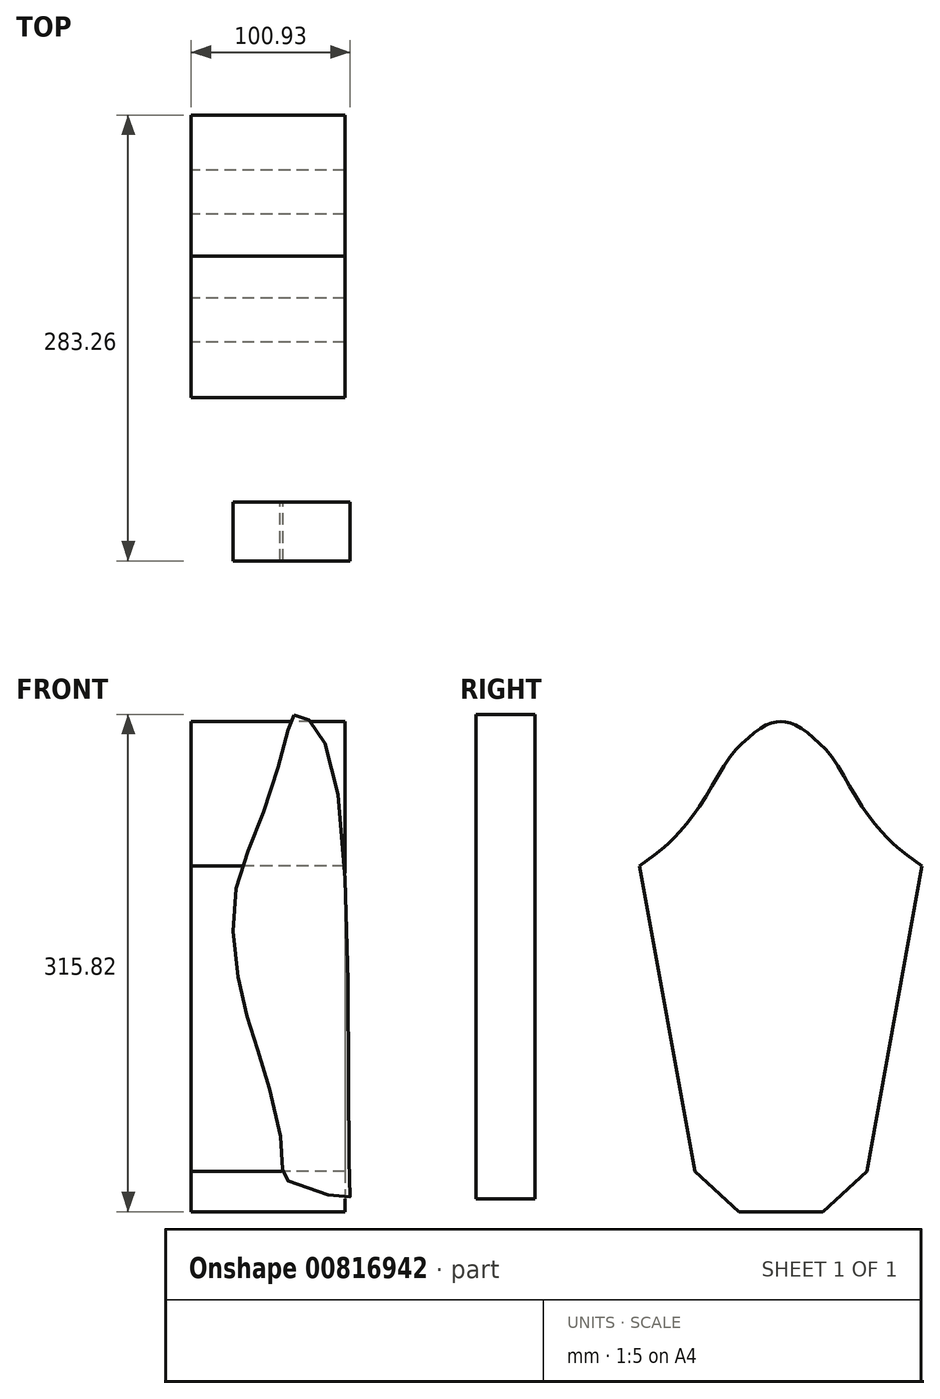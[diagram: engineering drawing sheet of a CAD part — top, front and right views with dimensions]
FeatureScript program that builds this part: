
annotation { "Feature Type Name" : "Feature", "Feature Type Description" : "" }
export const myFeature = defineFeature(function(context is Context, id is Id, definition is map)
    precondition{}
    {
        {
            var Q0;
            Q0=qCreatedBy(makeId("Right.planeOp"),FACE);
            var sketch = newSketch(context, id + "F0", { "sketchPlane" : qUnion([Q0])});
            skFitSpline(sketch, "E0", {"points": [v(0, 116.17) * mm, v(3.06, 115.78) * mm, v(7.67, 113.9) * mm, v(14.22, 108.94) * mm, v(22.25, 100.28) * mm, v(32.3, 83.46) * mm, v(42.34, 70.02) * mm, v(50.07, 62.3) * mm, v(59.84, 54.97) * mm], "startDerivative": vector(42.97, -3.15) * mm, "endDerivative": vector(75.08, -53.22) * mm});
            skLineSegment(sketch, "E1", {"start": v(59.84, 54.97) * mm, "end": v(36.42, -74.25) * mm});
            skLineSegment(sketch, "E2", {"start": v(36.42, -74.25) * mm, "end": v(17.78, -91.38) * mm});
            skLineSegment(sketch, "E3", {"start": v(17.78, -91.38) * mm, "end": v(0, -91.38) * mm});
            skLineSegment(sketch, "E4.MirrorCS", {"start": v(-59.84, 54.97) * mm, "end": v(-36.42, -74.25) * mm});
            skLineSegment(sketch, "E5.MirrorCS", {"start": v(-36.42, -74.25) * mm, "end": v(-17.78, -91.38) * mm});
            skLineSegment(sketch, "E6.MirrorCS", {"start": v(-17.78, -91.38) * mm, "end": v(0, -91.38) * mm});
            skFitSpline(sketch, "E7.MirrorCS", {"points": [v(0, 116.17) * mm, v(-3.06, 115.78) * mm, v(-7.67, 113.9) * mm, v(-14.22, 108.94) * mm, v(-22.25, 100.28) * mm, v(-32.3, 83.46) * mm, v(-42.34, 70.02) * mm, v(-50.07, 62.3) * mm, v(-59.84, 54.97) * mm], "startDerivative": vector(-42.97, -3.15) * mm, "endDerivative": vector(-75.08, -53.22) * mm});
            skSolve(sketch);
        }
        {
            var Q0;
            Q0=makeQuery(id+"F0.imprint","IMPRINT",FACE,{"disambiguationData":[TD([[makeQuery(id+"F0.imprint","IMPRINT",EDGE,{"derivedFrom":sQuery(id+"F0.wireOp",EDGE,"E0")}),-1.0]])]});
            extrude(context, id + "F1", {"entities" : qUnion([Q0]), "depth" : 65 * mm, "offsetDistance" : 25 * mm});
        }
        {
            var Q0;
            Q0=qCreatedBy(makeId("Front.planeOp"),FACE);
            cPlane(context, id + "F2", {"entities" : qUnion([Q0]), "cplaneType" : CPlaneType.OFFSET, "offset" : 75 * mm, "width" : 150 * mm, "height" : 150 * mm});
        }
        {
            var Q0;
            Q0=qCreatedBy(id+"F2.planeOp",FACE);
            var sketch = newSketch(context, id + "F3", { "sketchPlane" : qUnion([Q0])});
            skFitSpline(sketch, "E8", {"points": [v(31.28, 115.04) * mm, v(36.57, 113.68) * mm, v(49.83, 81.9) * mm, v(54.98, -86.37) * mm, v(53.81, -89.9) * mm, v(25.77, -80.55) * mm, v(26.37, -77.52) * mm, v(19.38, -38.05) * mm, v(10.13, -7.63) * mm, v(6.21, 37.7) * mm, v(18.81, 74.67) * mm, v(29.52, 111.7) * mm, v(31.28, 115.04) * mm]});
            skSolve(sketch);
        }
        {
            var Q0;
            Q0=qCreatedBy(makeId("Top.planeOp"),FACE);
            cPlane(context, id + "F4", {"entities" : qUnion([Q0]), "cplaneType" : CPlaneType.OFFSET, "offset" : 78 * mm, "oppositeDirection" : true, "width" : 150 * mm, "height" : 150 * mm});
        }
        {
            var Q0;
            Q0=qCreatedBy(id+"F4.planeOp",FACE);
            var sketch = newSketch(context, id + "F5", { "sketchPlane" : qUnion([Q0])});
            skCircle(sketch, "E9", {"center": v(36.86, 0) * mm, "radius": 3 * mm});
            skSolve(sketch);
        }
        {
            var Q0;
            Q0=qSketchRegion(id+"F5",true);
            extrude(context, id + "F6", {"entities" : qUnion([Q0]), "oppositeDirection" : true, "depth" : 27 * mm, "offsetDistance" : 25 * mm});
        }
        {
            var Q0;
            Q0=makeQuery(id+"F6.opExtrude","SWEPT_BODY",BODY,{"disambiguationData":[OSD([sQuery(id+"F5.wireOp",EDGE,"E9")])]});
            deleteBodies(context, id + "F7", {"entities" : qUnion([Q0])});
        }
        {
            var Q0;
            Q0=makeQuery(id+"F1.opExtrude","SWEPT_BODY",BODY,{"disambiguationData":[OSD([sQuery(id+"F0.wireOp",EDGE,"E0"),sQuery(id+"F0.wireOp",EDGE,"E1"),sQuery(id+"F0.wireOp",EDGE,"E2"),sQuery(id+"F0.wireOp",EDGE,"E3"),sQuery(id+"F0.wireOp",EDGE,"E4.MirrorCS"),sQuery(id+"F0.wireOp",EDGE,"E5.MirrorCS"),sQuery(id+"F0.wireOp",EDGE,"E6.MirrorCS"),sQuery(id+"F0.wireOp",EDGE,"E7.MirrorCS")])]});
            var Q1;
            Q1=qCreatedBy(makeId("Origin.pointOp"),VERTEX);
            transform(context, id + "F8", {"entities" : qUnion([Q0]), "transformType" : TransformType.SCALE_UNIFORMLY, "scale" : 1.5, "scalePoint" : qUnion([Q1]), "makeCopy" : false});
        }
        {
            var Q0;
            Q0=qCreatedBy(makeId("Front.planeOp"),FACE);
            cPlane(context, id + "F9", {"entities" : qUnion([Q0]), "cplaneType" : CPlaneType.OFFSET, "offset" : 104 * mm, "width" : 150 * mm, "height" : 150 * mm});
        }
        {
            var Q0;
            Q0=qCreatedBy(id+"F9.planeOp",FACE);
            var sketch = newSketch(context, id + "F10", { "sketchPlane" : qUnion([Q0])});
            skFitSpline(sketch, "E10", {"points": [v(43.42, 119.03) * mm, v(48.72, 117.67) * mm, v(61.97, 85.89) * mm, v(67.12, -82.39) * mm, v(65.95, -85.92) * mm, v(37.91, -76.56) * mm, v(38.52, -73.54) * mm, v(31.52, -34.07) * mm, v(22.28, -3.64) * mm, v(18.36, 41.68) * mm, v(30.95, 78.65) * mm, v(41.66, 115.7) * mm, v(43.42, 119.03) * mm]});
            skSolve(sketch);
        }
        {
            var Q0;
            Q0=makeQuery(id+"F10.imprint","IMPRINT",FACE,{"disambiguationData":[TD([[makeQuery(id+"F10.imprint","IMPRINT",EDGE,{"derivedFrom":sQuery(id+"F10.wireOp",EDGE,"E10")}),-1.0]])]});
            extrude(context, id + "F11", {"entities" : qUnion([Q0]), "depth" : 25 * mm, "offsetDistance" : 25 * mm});
        }
        {
            var Q0;
            Q0=makeQuery(id+"F11.opExtrude","SWEPT_BODY",BODY,{"disambiguationData":[OSD([sQuery(id+"F10.wireOp",EDGE,"E10")])]});
            var Q1;
            Q1=qCreatedBy(makeId("Origin.pointOp"),VERTEX);
            transform(context, id + "F12", {"entities" : qUnion([Q0]), "transformType" : TransformType.SCALE_UNIFORMLY, "scale" : 1.5, "scalePoint" : qUnion([Q1]), "makeCopy" : false});
        }
        {
            var Q0;
            Q0=qCreatedBy(makeId("Top.planeOp"),FACE);
            cPlane(context, id + "F13", {"entities" : qUnion([Q0]), "cplaneType" : CPlaneType.OFFSET, "offset" : 208 * mm, "width" : 150 * mm, "height" : 150 * mm});
        }
        {
            var Q0;
            Q0=makeQuery(id+"F11.opExtrude","CAP_FACE",FACE,{"disambiguationData":[OSD([sQuery(id+"F10.wireOp",EDGE,"E10")])],"isStart":true});
            extrude(context, id + "F14", {"entities" : qUnion([Q0]), "depth" : 259 * mm, "offsetDistance" : 25 * mm});
        }
        {
            var Q0;
            Q0=makeQuery(id+"F14.opExtrude","SWEPT_BODY",BODY,{"disambiguationData":[OSD([sQuery(id+"F10.wireOp",EDGE,"E10")])]});
            deleteBodies(context, id + "F15", {"entities" : qUnion([Q0])});
        }
    });
